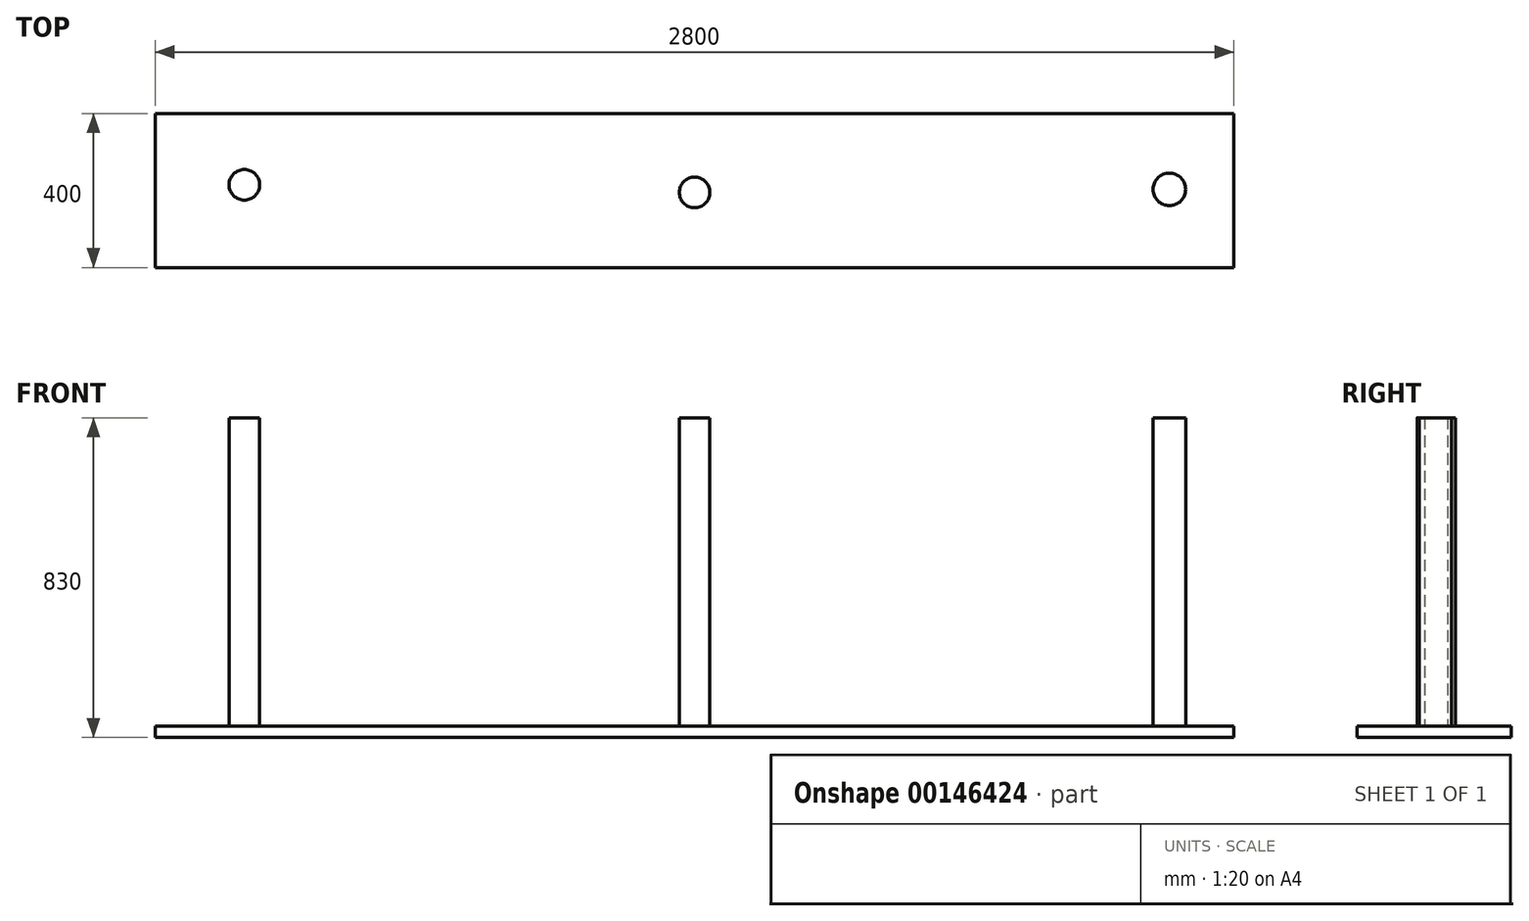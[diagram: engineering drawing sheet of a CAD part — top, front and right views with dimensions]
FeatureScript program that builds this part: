
annotation { "Feature Type Name" : "Feature", "Feature Type Description" : "" }
export const myFeature = defineFeature(function(context is Context, id is Id, definition is map)
    precondition{}
    {
        {
            var Q0;
            Q0=qCreatedBy(makeId("Top.planeOp"),FACE);
            var sketch = newSketch(context, id + "F0", { "sketchPlane" : qUnion([Q0])});
            skLineSegment(sketch, "E0.bottom", {"start": v(-2748.3, 374.1) * mm, "end": v(51.7, 374.1) * mm});
            skLineSegment(sketch, "E0.top", {"start": v(-2748.3, -25.9) * mm, "end": v(51.7, -25.9) * mm});
            skLineSegment(sketch, "E0.left", {"start": v(-2748.3, 374.1) * mm, "end": v(-2748.3, -25.9) * mm});
            skLineSegment(sketch, "E0.right", {"start": v(51.7, 374.1) * mm, "end": v(51.7, -25.9) * mm});
            skSolve(sketch);
        }
        {
            var Q0;
            Q0 = qSketchRegion(id + "F0", true);
            extrude(context, id + "F1", {"entities" : qUnion([Q0]), "depth" : 30 * mm});
        }
        {
            var Q0;
            Q0=makeQuery(id+"F1.opExtrude","CAP_FACE",FACE,{"disambiguationData":[OSD([sQuery(id+"F0.wireOp",EDGE,"E0.bottom"),sQuery(id+"F0.wireOp",EDGE,"E0.top"),sQuery(id+"F0.wireOp",EDGE,"E0.left"),sQuery(id+"F0.wireOp",EDGE,"E0.right")])],"isStart":false});
            var sketch = newSketch(context, id + "F2", { "sketchPlane" : qUnion([Q0])});
            skCircle(sketch, "E1", {"center": v(-2516.5, 189.02) * mm, "radius": 39.75 * mm});
            skCircle(sketch, "E2", {"center": v(-1347.98, 169.15) * mm, "radius": 39.75 * mm});
            skCircle(sketch, "E3", {"center": v(-115.87, 177.1) * mm, "radius": 42.25 * mm});
            skSolve(sketch);
        }
        {
            var Q0;
            Q0 = qSketchRegion(id + "F2", true);
            extrude(context, id + "F3", {"entities" : qUnion([Q0]), "operationType" : NewBodyOperationType.ADD, "depth" : 800 * mm});
        }
    });
